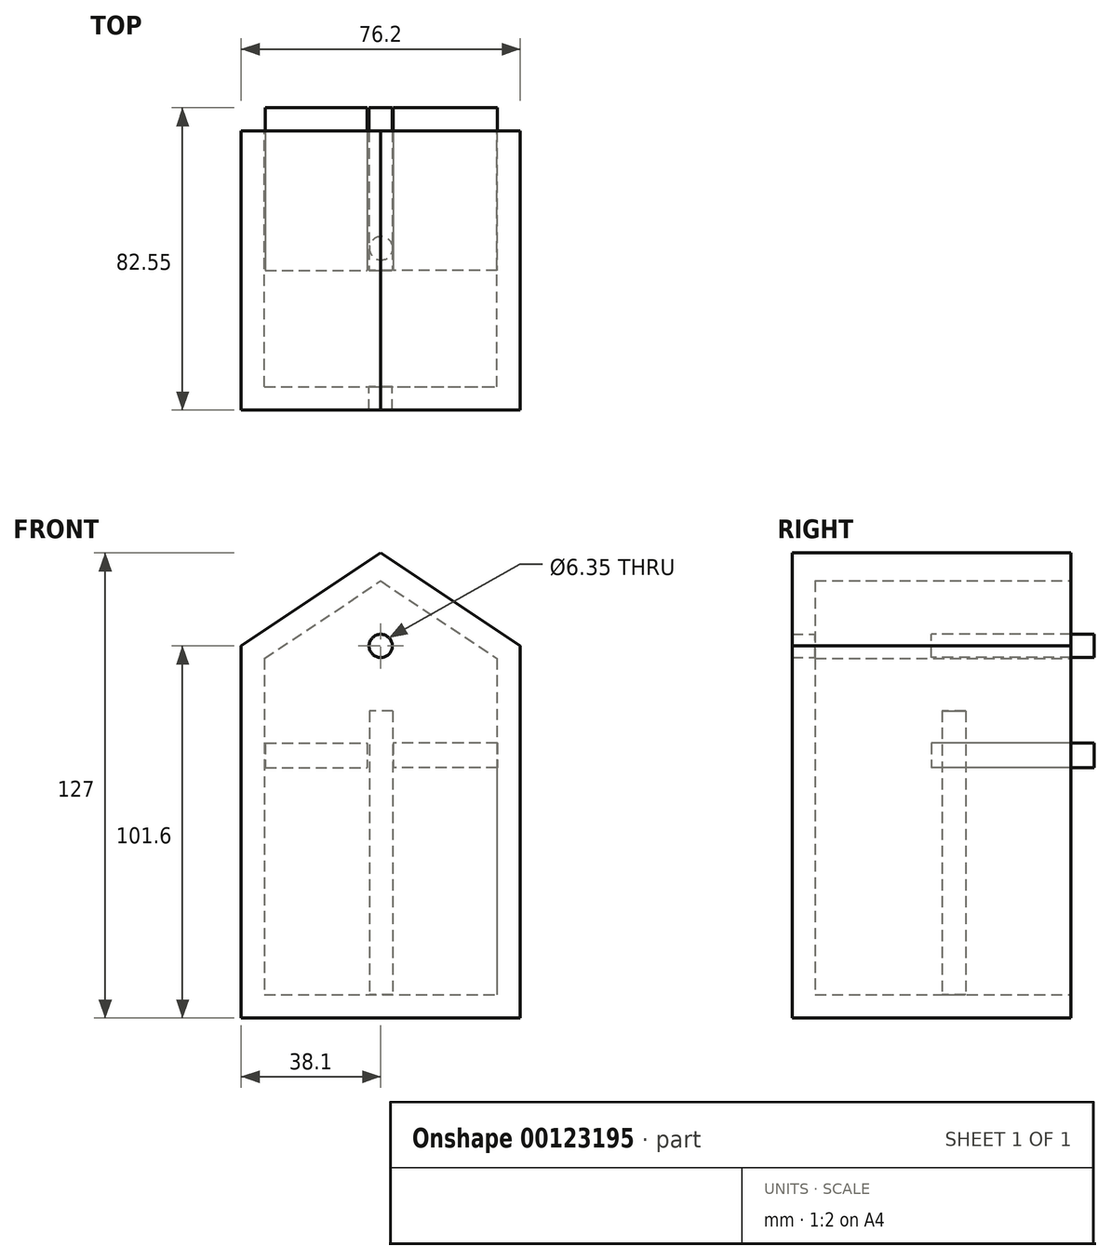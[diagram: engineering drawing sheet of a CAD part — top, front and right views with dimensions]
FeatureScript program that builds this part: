
annotation { "Feature Type Name" : "Feature", "Feature Type Description" : "" }
export const myFeature = defineFeature(function(context is Context, id is Id, definition is map)
    precondition{}
    {
        {
            var Q0;
            Q0=qCreatedBy(makeId("Front.planeOp"),FACE);
            var sketch = newSketch(context, id + "F0", { "sketchPlane" : qUnion([Q0])});
            skLineSegment(sketch, "E0.bottom", {"start": v(-38.1, 50.8) * mm, "end": v(38.1, 50.8) * mm, "construction": true});
            skLineSegment(sketch, "E0.top", {"start": v(-38.1, -50.8) * mm, "end": v(38.1, -50.8) * mm});
            skLineSegment(sketch, "E0.left", {"start": v(-38.1, 50.8) * mm, "end": v(-38.1, -50.8) * mm});
            skLineSegment(sketch, "E0.right", {"start": v(38.1, 50.8) * mm, "end": v(38.1, -50.8) * mm});
            skLineSegment(sketch, "E1", {"start": v(0, 50.8) * mm, "end": v(0, -50.8) * mm, "construction": true});
            skLineSegment(sketch, "E2", {"start": v(-38.1, 50.8) * mm, "end": v(0, 76.2) * mm});
            skLineSegment(sketch, "E3", {"start": v(0, 76.2) * mm, "end": v(38.1, 50.8) * mm});
            skSolve(sketch);
        }
        {
            var Q0;
            Q0 = qSketchRegion(id + "F0", true);
            extrude(context, id + "F1", {"entities" : qUnion([Q0]), "endBound" : BoundingType.SYMMETRIC, "depth" : 76.2 * mm});
        }
        {
            var Q0;
            Q0=makeQuery(id+"F1.opExtrude","CAP_FACE",FACE,{"disambiguationData":[OSD([sQuery(id+"F0.wireOp",EDGE,"E0.top"),sQuery(id+"F0.wireOp",EDGE,"E0.left"),sQuery(id+"F0.wireOp",EDGE,"E0.right"),sQuery(id+"F0.wireOp",EDGE,"E2"),sQuery(id+"F0.wireOp",EDGE,"E3")])],"isStart":true});
            shell(context, id + "F2", {"entities" : qUnion([Q0]), "thickness" : 6.35 * mm});
        }
        {
            var Q0;
            Q0=makeQuery(id+"F0.imprint","IMPRINT",FACE,{"disambiguationData":[TD([[makeQuery(id+"F0.imprint","IMPRINT",EDGE,{"derivedFrom":sQuery(id+"F0.wireOp",EDGE,"E0.top")}),1.0]])]});
            var sketch = newSketch(context, id + "F3", { "sketchPlane" : qUnion([Q0])});
            skLineSegment(sketch, "E4.bottom", {"start": v(31.85, 24.31) * mm, "end": v(3.36, 24.31) * mm});
            skLineSegment(sketch, "E4.top", {"start": v(31.85, 17.54) * mm, "end": v(3.36, 17.54) * mm});
            skLineSegment(sketch, "E4.left", {"start": v(31.85, 24.31) * mm, "end": v(31.85, 17.54) * mm});
            skLineSegment(sketch, "E4.right", {"start": v(3.36, 24.31) * mm, "end": v(3.36, 17.54) * mm});
            skLineSegment(sketch, "E5.bottom", {"start": v(-31.54, 24.31) * mm, "end": v(-3.74, 24.31) * mm});
            skLineSegment(sketch, "E5.top", {"start": v(-31.54, 17.54) * mm, "end": v(-3.74, 17.54) * mm});
            skLineSegment(sketch, "E5.left", {"start": v(-31.54, 24.31) * mm, "end": v(-31.54, 17.54) * mm});
            skLineSegment(sketch, "E5.right", {"start": v(-3.74, 24.31) * mm, "end": v(-3.74, 17.54) * mm});
            skSolve(sketch);
        }
        {
            var Q0;
            Q0=sQuery(id+"F3.wireOp",EDGE,"E4.bottom");
            var Q1;
            Q1=sQuery(id+"F3.wireOp",EDGE,"E4.right");
            var Q2;
            Q2=sQuery(id+"F3.wireOp",EDGE,"E4.top");
            var Q3;
            Q3=sQuery(id+"F3.wireOp",EDGE,"E4.left");
            var Q4;
            Q4=sQuery(id+"F3.wireOp",EDGE,"E5.right");
            var Q5;
            Q5=sQuery(id+"F3.wireOp",EDGE,"E5.bottom");
            var Q6;
            Q6=sQuery(id+"F3.wireOp",EDGE,"E5.top");
            var Q7;
            Q7=sQuery(id+"F3.wireOp",EDGE,"E5.left");
            extrude(context, id + "F4", {"bodyType" : ToolBodyType.SURFACE, "surfaceEntities" : qUnion([Q0, Q1, Q2, Q3, Q4, Q5, Q6, Q7]), "endBound" : BoundingType.SYMMETRIC, "oppositeDirection" : true, "depth" : 76.2 * mm});
        }
        {
            var Q0;
            Q0=makeQuery(id+"F2.opShell","OFFSET_FACE",FACE,{"disambiguationData":[OSD([sQuery(id+"F0.wireOp",EDGE,"E0.top")])]});
            var sketch = newSketch(context, id + "F5", { "sketchPlane" : qUnion([Q0])});
            skCircle(sketch, "E6", {"center": v(0.09, 6.08) * mm, "radius": 3.2 * mm});
            skSolve(sketch);
        }
        {
            var Q0;
            Q0 = qSketchRegion(id + "F5", true);
            extrude(context, id + "F6", {"entities" : qUnion([Q0]), "operationType" : NewBodyOperationType.ADD, "depth" : 77.51 * mm});
        }
        {
            var Q0;
            Q0=makeQuery(id+"F3.imprint","IMPRINT",FACE,{"disambiguationData":[TD([[makeQuery(id+"F3.imprint","IMPRINT",EDGE,{"derivedFrom":sQuery(id+"F3.wireOp",EDGE,"E4.bottom")}),-1.0]])]});
            var sketch = newSketch(context, id + "F7", { "sketchPlane" : qUnion([Q0])});
            skCircle(sketch, "E7", {"center": v(0, 50.8) * mm, "radius": 3.18 * mm});
            skSolve(sketch);
        }
        {
            var Q0;
            Q0 = qSketchRegion(id + "F7", true);
            extrude(context, id + "F8", {"entities" : qUnion([Q0]), "operationType" : NewBodyOperationType.REMOVE, "endBound" : BoundingType.THROUGH_ALL, "depth" : 50.8 * mm});
        }
        {
            var Q0;
            Q0 = qSketchRegion(id + "F7", true);
            extrude(context, id + "F10", {"entities" : qUnion([Q0]), "oppositeDirection" : true, "depth" : 44.45 * mm});
        }
        {
            var Q0;
            Q0 = qSketchRegion(id + "F3", true);
            extrude(context, id + "F12", {"entities" : qUnion([Q0]), "operationType" : NewBodyOperationType.ADD, "oppositeDirection" : true, "depth" : 44.45 * mm});
        }
        {
            var Q0;
            Q0 = qConstructionFilter(qBodyType(qCreatedBy(id + "F5" ,EDGE), BodyType.WIRE), ConstructionObject.NO);
            extrude(context, id + "F13", {"bodyType" : ToolBodyType.SURFACE, "surfaceEntities" : qUnion([Q0]), "oppositeDirection" : true, "depth" : 31.75 * mm});
        }
    });
